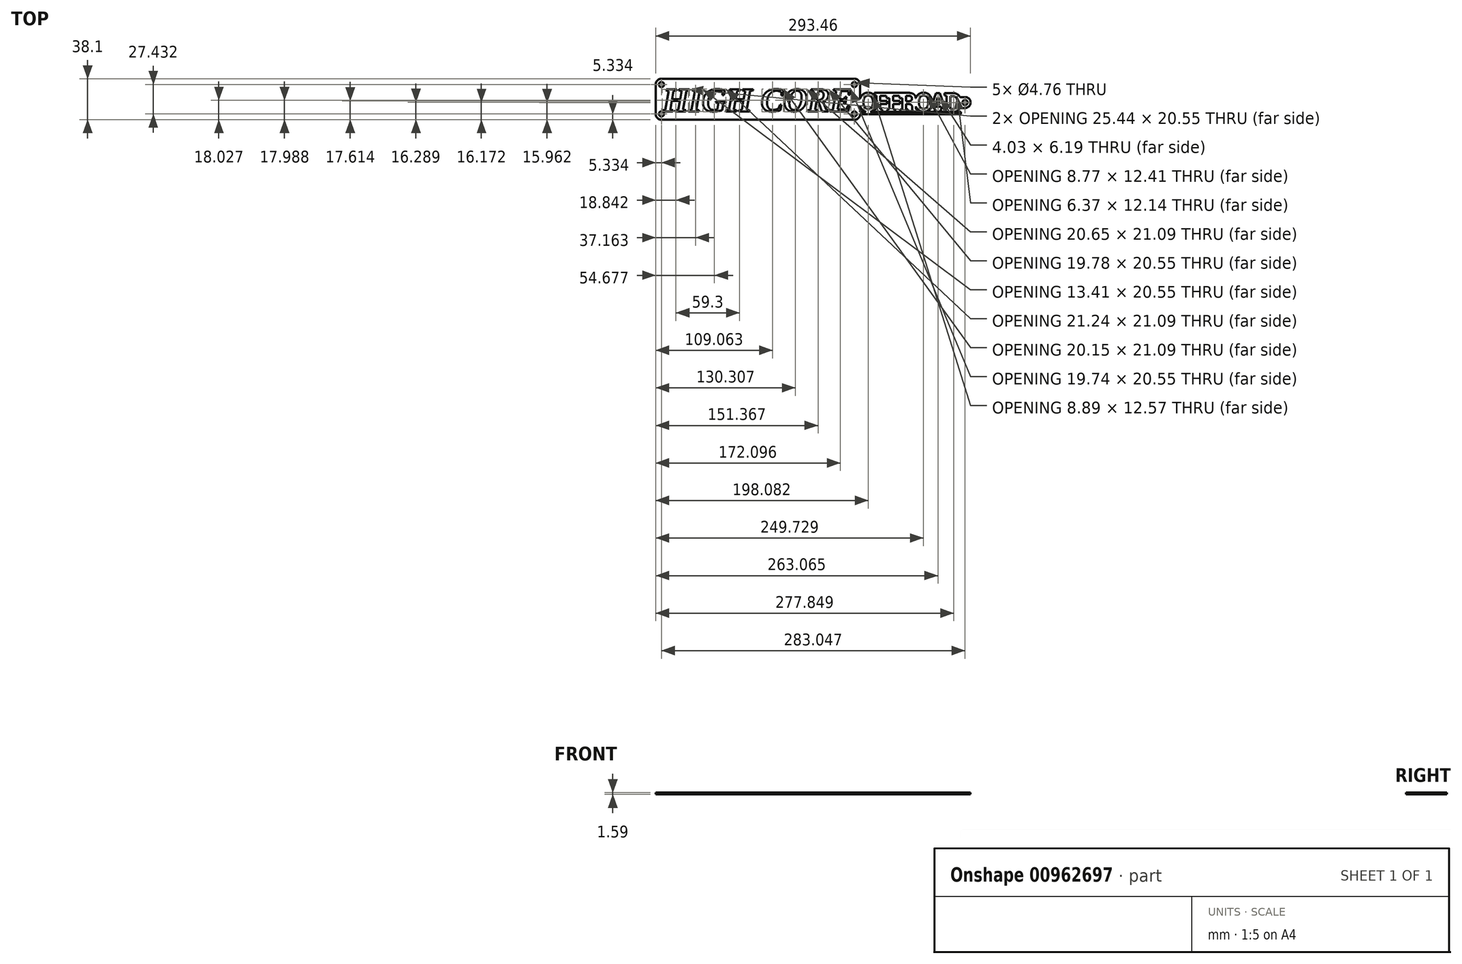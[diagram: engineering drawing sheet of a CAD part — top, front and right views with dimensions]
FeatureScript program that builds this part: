
annotation { "Feature Type Name" : "Feature", "Feature Type Description" : "" }
export const myFeature = defineFeature(function(context is Context, id is Id, definition is map)
    precondition{}
    {
        {
            var Q0;
            Q0=qCreatedBy(makeId("Top.planeOp"),FACE);
            var sketch = newSketch(context, id + "F0", { "sketchPlane" : qUnion([Q0])});
            skLineSegment(sketch, "E0.bottom", {"start": v(95.25, -19.05) * mm, "end": v(-95.25, -19.05) * mm});
            skLineSegment(sketch, "E0.top", {"start": v(95.25, 19.05) * mm, "end": v(-95.25, 19.05) * mm});
            skLineSegment(sketch, "E0.left", {"start": v(95.25, -19.05) * mm, "end": v(95.25, 19.05) * mm});
            skLineSegment(sketch, "E0.right", {"start": v(-95.25, -19.05) * mm, "end": v(-95.25, 19.05) * mm});
            skPoint(sketch, "E0.middle", {"position": v(0, 0) * mm});
            skSolve(sketch);
        }
        {
            var Q0;
            Q0=makeQuery(id+"F0.imprint","IMPRINT",FACE,{"disambiguationData":[TD([[makeQuery(id+"F0.imprint","IMPRINT",EDGE,{"derivedFrom":sQuery(id+"F0.wireOp",EDGE,"E0.bottom")}),-1.0]])]});
            extrude(context, id + "F1", {"entities" : qUnion([Q0]), "depth" : 1.59 * mm, "offsetDistance" : 25.4 * mm});
        }
        {
            var Q0;
            Q0=makeQuery(id+"F1.opExtrude","CAP_FACE",FACE,{"disambiguationData":[OSD([sQuery(id+"F0.wireOp",EDGE,"E0.bottom"),sQuery(id+"F0.wireOp",EDGE,"E0.top"),sQuery(id+"F0.wireOp",EDGE,"E0.left"),sQuery(id+"F0.wireOp",EDGE,"E0.right")])],"isStart":false});
            var sketch = newSketch(context, id + "F2", { "sketchPlane" : qUnion([Q0])});
            skText(sketch, "E1", { "text": "HIGH CORE", "fontName": "Tinos-BoldItalic.ttf"});
            skPoint(sketch, "E2", {"position": v(0, 0) * mm});
            skLineSegment(sketch, "E3", {"start": v(-89.92, 0) * mm, "end": v(0, 0) * mm, "construction": true});
            skLineSegment(sketch, "E4", {"start": v(0, 0) * mm, "end": v(89.92, 0) * mm, "construction": true});
            skLineSegment(sketch, "E5", {"start": v(-95.25, 19.05) * mm, "end": v(-88.39, 12.19) * mm, "construction": true});
            skLineSegment(sketch, "E6", {"start": v(-89.92, 0) * mm, "end": v(-89.92, 13.72) * mm, "construction": true});
            skCircle(sketch, "E7", {"center": v(-89.92, 13.72) * mm, "radius": 2.38 * mm});
            skCircle(sketch, "E8.MirrorC", {"center": v(-89.92, -13.72) * mm, "radius": 2.38 * mm});
            skCircle(sketch, "E9.MirrorC", {"center": v(89.92, 13.72) * mm, "radius": 2.38 * mm});
            skCircle(sketch, "E10.MirrorC", {"center": v(89.92, -13.72) * mm, "radius": 2.38 * mm});
            const initialGuessF2  = {"E1": [-0.0889, -0.0113, 1, 0, 0.0226]};
            skSetInitialGuess(sketch, initialGuessF2);
            skSolve(sketch);
        }
        {
            var Q0;
            Q0=qSketchRegion(id+"F2",true);
            extrude(context, id + "F3", {"entities" : qUnion([Q0]), "operationType" : NewBodyOperationType.REMOVE, "oppositeDirection" : true, "depth" : 25.4 * mm, "offsetDistance" : 25.4 * mm});
        }
        {
            var Q0;
            Q0=makeQuery(id+"F1.opExtrude","SWEPT_EDGE",EDGE,{"disambiguationData":[OSD([sQuery(id+"F0.wireOp",EDGE,"E0.top"),sQuery(id+"F0.wireOp",EDGE,"E0.right")])]});
            var Q1;
            Q1=makeQuery(id+"F1.opExtrude","SWEPT_EDGE",EDGE,{"disambiguationData":[OSD([sQuery(id+"F0.wireOp",EDGE,"E0.bottom"),sQuery(id+"F0.wireOp",EDGE,"E0.right")])]});
            var Q2;
            Q2=makeQuery(id+"F1.opExtrude","SWEPT_EDGE",EDGE,{"disambiguationData":[OSD([sQuery(id+"F0.wireOp",EDGE,"E0.top"),sQuery(id+"F0.wireOp",EDGE,"E0.left")])]});
            var Q3;
            Q3=makeQuery(id+"F1.opExtrude","SWEPT_EDGE",EDGE,{"disambiguationData":[OSD([sQuery(id+"F0.wireOp",EDGE,"E0.bottom"),sQuery(id+"F0.wireOp",EDGE,"E0.left")])]});
            fillet(context, id + "F4", {"entities" : qUnion([Q0, Q1, Q2, Q3]), "radius" : 5.08 * mm, "tangentPropagation" : true, "allowEdgeOverflow" : false});
        }
        {
            var Q0;
            Q0=makeQuery(id+"F1.opExtrude","CAP_FACE",FACE,{"disambiguationData":[OSD([sQuery(id+"F0.wireOp",EDGE,"E0.bottom"),sQuery(id+"F0.wireOp",EDGE,"E0.top"),sQuery(id+"F0.wireOp",EDGE,"E0.left"),sQuery(id+"F0.wireOp",EDGE,"E0.right")])],"isStart":false});
            var sketch = newSketch(context, id + "F5", { "sketchPlane" : qUnion([Q0])});
            skPoint(sketch, "E11", {"position": v(93.37, -3.45) * mm});
            skText(sketch, "E12", { "text": "O", "fontName": "RobotoSlab-Bold.ttf"});
            skText(sketch, "E13", { "text": "F", "fontName": "RobotoSlab-Bold.ttf"});
            skText(sketch, "E14", { "text": "F", "fontName": "RobotoSlab-Bold.ttf"});
            skText(sketch, "E15", { "text": "R", "fontName": "RobotoSlab-Bold.ttf"});
            skText(sketch, "E16", { "text": "O", "fontName": "RobotoSlab-Bold.ttf"});
            skText(sketch, "E17", { "text": "A", "fontName": "RobotoSlab-Bold.ttf"});
            skText(sketch, "E18", { "text": "D", "fontName": "RobotoSlab-Bold.ttf"});
            skLineSegment(sketch, "E19", {"start": v(87.12, -11.65) * mm, "end": v(189.23, -11.65) * mm});
            skLineSegment(sketch, "E20.0", {"start": v(95.25, -13.97) * mm, "end": v(95.25, 13.97) * mm});
            skLineSegment(sketch, "E21", {"start": v(95.25, -13.97) * mm, "end": v(189.23, -13.97) * mm});
            skLineSegment(sketch, "E22", {"start": v(189.23, -11.65) * mm, "end": v(189.23, -13.97) * mm});
            skLineSegment(sketch, "E23", {"start": v(95.25, -13.97) * mm, "end": v(95.25, -11.65) * mm});
            skLineSegment(sketch, "E24", {"start": v(95.25, -11.65) * mm, "end": v(189.23, -11.65) * mm});
            const initialGuessF5  = {"E12": [0.09406, -0.01165, 1, 0, 0.01778], "E13": [0.10804, -0.01165, 1, 0, 0.01778], "E14": [0.12013, -0.01165, 1, 0, 0.01778], "E15": [0.1322, -0.01165, 1, 0, 0.01778], "E16": [0.14582, -0.01142, 1, 0, 0.01755], "E17": [0.15894, -0.01186, 1, 0, 0.01778], "E18": [0.17335, -0.01186, 1, 0, 0.01778]};
            skSetInitialGuess(sketch, initialGuessF5);
            skSolve(sketch);
        }
        {
            var Q0;
            {var subQ2=sQuery(id+"F5.wireOp",EDGE,"E17.sketch_text.stroke-5");Q0=makeQuery(id+"F5.imprint","IMPRINT",FACE,{"disambiguationData":[TD([[makeQuery(id+"F5.imprint","IMPRINT",EDGE,{"derivedFrom":subQ2}),-1.0]])]});}
            var Q1;
            {var subQ6=sQuery(id+"F5.wireOp",EDGE,"E17.sketch_text.stroke-5");Q1=makeQuery(id+"F5.imprint","IMPRINT",FACE,{"disambiguationData":[TD([[makeQuery(id+"F5.imprint","IMPRINT",EDGE,{"derivedFrom":subQ6}),1.0]])]});}
            var Q2;
            {var subQ15=sQuery(id+"F5.wireOp",EDGE,"E17.sketch_text.stroke-2");Q2=makeQuery(id+"F5.imprint","IMPRINT",FACE,{"disambiguationData":[TD([[makeQuery(id+"F5.imprint","IMPRINT",EDGE,{"derivedFrom":subQ15}),-1.0]])]});}
            var Q3;
            {var subQ0=sQuery(id+"F5.wireOp",EDGE,"E16.sketch_text.stroke-1");var subQ1=sQuery(id+"F5.wireOp",EDGE,"E16.sketch_text.stroke-0");var subQ2=makeQuery(id+"F5.imprint","INTERSECT",VERTEX,{"derivedFrom":[subQ1,subQ0]});Q3=makeQuery(id+"F5.imprint","IMPRINT",FACE,{"disambiguationData":[TD([[makeQuery(id+"F5.imprint","IMPRINT",EDGE,{"disambiguationData":[TD([[subQ2,1.0]])],"derivedFrom":subQ1}),1.0]])]});}
            var Q4;
            {var subQ0=sQuery(id+"F5.wireOp",EDGE,"E17.sketch_text.stroke-15");var subQ1=sQuery(id+"F5.wireOp",EDGE,"E16.sketch_text.stroke-1");var subQ2=makeQuery(id+"F5.imprint","INTERSECT",VERTEX,{"derivedFrom":[subQ1,subQ0]});Q4=makeQuery(id+"F5.imprint","IMPRINT",FACE,{"disambiguationData":[TD([[makeQuery(id+"F5.imprint","IMPRINT",EDGE,{"disambiguationData":[TD([[subQ2,1.0]])],"derivedFrom":subQ1}),-1.0]])]});}
            var Q5;
            {var subQ9=sQuery(id+"F5.wireOp",EDGE,"E16.sketch_text.stroke-4");Q5=makeQuery(id+"F5.imprint","IMPRINT",FACE,{"disambiguationData":[TD([[makeQuery(id+"F5.imprint","IMPRINT",EDGE,{"derivedFrom":subQ9}),-1.0]])]});}
            var Q6;
            {var subQ0=sQuery(id+"F5.wireOp",EDGE,"E17.sketch_text.stroke-1");var subQ1=sQuery(id+"F5.wireOp",EDGE,"E16.sketch_text.stroke-0");var subQ2=makeQuery(id+"F5.imprint","INTERSECT",VERTEX,{"disambiguationData":[OD(0.0)],"derivedFrom":[subQ1,subQ0]});Q6=makeQuery(id+"F5.imprint","IMPRINT",FACE,{"disambiguationData":[TD([[makeQuery(id+"F5.imprint","IMPRINT",EDGE,{"disambiguationData":[TD([[subQ2,-1.0]])],"derivedFrom":subQ1}),-1.0]])]});}
            var Q7;
            {var subQ7=sQuery(id+"F5.wireOp",EDGE,"E14.sketch_text.stroke-5");Q7=makeQuery(id+"F5.imprint","IMPRINT",FACE,{"disambiguationData":[TD([[makeQuery(id+"F5.imprint","IMPRINT",EDGE,{"derivedFrom":subQ7}),1.0]])]});}
            var Q8;
            {var subQ0=sQuery(id+"F5.wireOp",EDGE,"E15.sketch_text.stroke-2");var subQ1=sQuery(id+"F5.wireOp",EDGE,"E15.sketch_text.stroke-1");var subQ2=makeQuery(id+"F5.imprint","INTERSECT",VERTEX,{"derivedFrom":[subQ1,subQ0]});Q8=makeQuery(id+"F5.imprint","IMPRINT",FACE,{"disambiguationData":[TD([[makeQuery(id+"F5.imprint","IMPRINT",EDGE,{"disambiguationData":[TD([[subQ2,1.0]])],"derivedFrom":subQ1}),-1.0]])]});}
            var Q9;
            {var subQ0=sQuery(id+"F5.wireOp",EDGE,"E16.sketch_text.stroke-3");var subQ1=sQuery(id+"F5.wireOp",EDGE,"E15.sketch_text.stroke-5");var subQ2=makeQuery(id+"F5.imprint","INTERSECT",VERTEX,{"disambiguationData":[OD(0.0)],"derivedFrom":[subQ1,subQ0]});Q9=makeQuery(id+"F5.imprint","IMPRINT",FACE,{"disambiguationData":[TD([[makeQuery(id+"F5.imprint","IMPRINT",EDGE,{"disambiguationData":[TD([[subQ2,-1.0]])],"derivedFrom":subQ1}),-1.0]])]});}
            var Q10;
            {var subQ2=sQuery(id+"F5.wireOp",EDGE,"E14.sketch_text.stroke-5");Q10=makeQuery(id+"F5.imprint","IMPRINT",FACE,{"disambiguationData":[TD([[makeQuery(id+"F5.imprint","IMPRINT",EDGE,{"derivedFrom":subQ2}),-1.0]])]});}
            var Q11;
            {var subQ1=sQuery(id+"F5.wireOp",EDGE,"E13.sketch_text.stroke-5");Q11=makeQuery(id+"F5.imprint","IMPRINT",FACE,{"disambiguationData":[TD([[makeQuery(id+"F5.imprint","IMPRINT",EDGE,{"derivedFrom":subQ1}),1.0]])]});}
            var Q12;
            {var subQ2=sQuery(id+"F5.wireOp",EDGE,"E13.sketch_text.stroke-5");Q12=makeQuery(id+"F5.imprint","IMPRINT",FACE,{"disambiguationData":[TD([[makeQuery(id+"F5.imprint","IMPRINT",EDGE,{"derivedFrom":subQ2}),-1.0]])]});}
            var Q13;
            {var subQ8=sQuery(id+"F5.wireOp",EDGE,"E12.sketch_text.stroke-9");Q13=makeQuery(id+"F5.imprint","IMPRINT",FACE,{"disambiguationData":[TD([[makeQuery(id+"F5.imprint","IMPRINT",EDGE,{"derivedFrom":subQ8}),1.0]])]});}
            var Q14;
            {var subQ0=sQuery(id+"F5.wireOp",EDGE,"E12.sketch_text.stroke-6");Q14=makeQuery(id+"F5.imprint","IMPRINT",FACE,{"disambiguationData":[TD([[makeQuery(id+"F5.imprint","IMPRINT",EDGE,{"derivedFrom":subQ0}),-1.0]])]});}
            var Q15;
            {var subQ5=sQuery(id+"F5.wireOp",EDGE,"E15.sketch_text.stroke-3");Q15=makeQuery(id+"F5.imprint","IMPRINT",FACE,{"disambiguationData":[TD([[makeQuery(id+"F5.imprint","IMPRINT",EDGE,{"derivedFrom":subQ5}),1.0]])]});}
            var Q16;
            Q16=makeQuery(id+"F5.imprint","IMPRINT",FACE,{"disambiguationData":[TD([[makeQuery(id+"F5.imprint","IMPRINT",EDGE,{"derivedFrom":sQuery(id+"F5.wireOp",EDGE,"E18.sketch_text.stroke-0")}),-1.0]])]});
            var Q17;
            {var subQ3=sQuery(id+"F5.wireOp",EDGE,"E17.sketch_text.stroke-4");var subQ5=sQuery(id+"F5.wireOp",EDGE,"E17.sketch_text.stroke-5");var subQ6=makeQuery(id+"F5.imprint","INTERSECT",VERTEX,{"derivedFrom":[subQ3,subQ5]});Q17=makeQuery(id+"F5.imprint","IMPRINT",FACE,{"disambiguationData":[TD([[makeQuery(id+"F5.imprint","IMPRINT",EDGE,{"disambiguationData":[TD([[subQ6,1.0]])],"derivedFrom":subQ3}),-1.0]])]});}
            extrude(context, id + "F6", {"entities" : qUnion([Q0, Q1, Q2, Q3, Q4, Q5, Q6, Q7, Q8, Q9, Q10, Q11, Q12, Q13, Q14, Q15, Q16, Q17]), "operationType" : NewBodyOperationType.ADD, "oppositeDirection" : true, "depth" : 1.59 * mm, "offsetDistance" : 25.4 * mm});
        }
        {
            var Q0;
            Q0=makeQuery(id+"F6.opExtrude","CAP_FACE",FACE,{"disambiguationData":[OSD([sQuery(id+"F5.wireOp",EDGE,"E12.sketch_text.stroke-0"),sQuery(id+"F5.wireOp",EDGE,"E12.sketch_text.stroke-8"),sQuery(id+"F5.wireOp",EDGE,"E12.sketch_text.stroke-9"),sQuery(id+"F5.wireOp",EDGE,"E13.sketch_text.stroke-0"),sQuery(id+"F5.wireOp",EDGE,"E13.sketch_text.stroke-1"),sQuery(id+"F5.wireOp",EDGE,"E13.sketch_text.stroke-2"),sQuery(id+"F5.wireOp",EDGE,"E13.sketch_text.stroke-3"),sQuery(id+"F5.wireOp",EDGE,"E13.sketch_text.stroke-4"),sQuery(id+"F5.wireOp",EDGE,"E13.sketch_text.stroke-6"),sQuery(id+"F5.wireOp",EDGE,"E13.sketch_text.stroke-7"),sQuery(id+"F5.wireOp",EDGE,"E13.sketch_text.stroke-8"),sQuery(id+"F5.wireOp",EDGE,"E13.sketch_text.stroke-9"),sQuery(id+"F5.wireOp",EDGE,"E13.sketch_text.stroke-10"),sQuery(id+"F5.wireOp",EDGE,"E13.sketch_text.stroke-11"),sQuery(id+"F5.wireOp",EDGE,"E13.sketch_text.stroke-12"),sQuery(id+"F5.wireOp",EDGE,"E13.sketch_text.stroke-13"),sQuery(id+"F5.wireOp",EDGE,"E13.sketch_text.stroke-14"),sQuery(id+"F5.wireOp",EDGE,"E13.sketch_text.stroke-15"),sQuery(id+"F5.wireOp",EDGE,"E13.sketch_text.stroke-17"),sQuery(id+"F5.wireOp",EDGE,"E14.sketch_text.stroke-0"),sQuery(id+"F5.wireOp",EDGE,"E14.sketch_text.stroke-1"),sQuery(id+"F5.wireOp",EDGE,"E14.sketch_text.stroke-4"),sQuery(id+"F5.wireOp",EDGE,"E14.sketch_text.stroke-6"),sQuery(id+"F5.wireOp",EDGE,"E14.sketch_text.stroke-7"),sQuery(id+"F5.wireOp",EDGE,"E14.sketch_text.stroke-8"),sQuery(id+"F5.wireOp",EDGE,"E14.sketch_text.stroke-9"),sQuery(id+"F5.wireOp",EDGE,"E14.sketch_text.stroke-10"),sQuery(id+"F5.wireOp",EDGE,"E14.sketch_text.stroke-11"),sQuery(id+"F5.wireOp",EDGE,"E14.sketch_text.stroke-12"),sQuery(id+"F5.wireOp",EDGE,"E14.sketch_text.stroke-13"),sQuery(id+"F5.wireOp",EDGE,"E14.sketch_text.stroke-14"),sQuery(id+"F5.wireOp",EDGE,"E14.sketch_text.stroke-15"),sQuery(id+"F5.wireOp",EDGE,"E14.sketch_text.stroke-17"),sQuery(id+"F5.wireOp",EDGE,"E15.sketch_text.stroke-0"),sQuery(id+"F5.wireOp",EDGE,"E15.sketch_text.stroke-1"),sQuery(id+"F5.wireOp",EDGE,"E15.sketch_text.stroke-5"),sQuery(id+"F5.wireOp",EDGE,"E15.sketch_text.stroke-6"),sQuery(id+"F5.wireOp",EDGE,"E15.sketch_text.stroke-7"),sQuery(id+"F5.wireOp",EDGE,"E15.sketch_text.stroke-8"),sQuery(id+"F5.wireOp",EDGE,"E15.sketch_text.stroke-9"),sQuery(id+"F5.wireOp",EDGE,"E15.sketch_text.stroke-10"),sQuery(id+"F5.wireOp",EDGE,"E15.sketch_text.stroke-12"),sQuery(id+"F5.wireOp",EDGE,"E15.sketch_text.stroke-13"),sQuery(id+"F5.wireOp",EDGE,"E15.sketch_text.stroke-14"),sQuery(id+"F5.wireOp",EDGE,"E15.sketch_text.stroke-15"),sQuery(id+"F5.wireOp",EDGE,"E15.sketch_text.stroke-16"),sQuery(id+"F5.wireOp",EDGE,"E15.sketch_text.stroke-17"),sQuery(id+"F5.wireOp",EDGE,"E15.sketch_text.stroke-18"),sQuery(id+"F5.wireOp",EDGE,"E15.sketch_text.stroke-19"),sQuery(id+"F5.wireOp",EDGE,"E15.sketch_text.stroke-20"),sQuery(id+"F5.wireOp",EDGE,"E15.sketch_text.stroke-22"),sQuery(id+"F5.wireOp",EDGE,"E15.sketch_text.stroke-23"),sQuery(id+"F5.wireOp",EDGE,"E15.sketch_text.stroke-24"),sQuery(id+"F5.wireOp",EDGE,"E15.sketch_text.stroke-27"),sQuery(id+"F5.wireOp",EDGE,"E15.sketch_text.stroke-28"),sQuery(id+"F5.wireOp",EDGE,"E15.sketch_text.stroke-29"),sQuery(id+"F5.wireOp",EDGE,"E15.sketch_text.stroke-30"),sQuery(id+"F5.wireOp",EDGE,"E15.sketch_text.stroke-31"),sQuery(id+"F5.wireOp",EDGE,"E15.sketch_text.stroke-32"),sQuery(id+"F5.wireOp",EDGE,"E15.sketch_text.stroke-33"),sQuery(id+"F5.wireOp",EDGE,"E15.sketch_text.stroke-34"),sQuery(id+"F5.wireOp",EDGE,"E15.sketch_text.stroke-35"),sQuery(id+"F5.wireOp",EDGE,"E16.sketch_text.stroke-0"),sQuery(id+"F5.wireOp",EDGE,"E16.sketch_text.stroke-1"),sQuery(id+"F5.wireOp",EDGE,"E16.sketch_text.stroke-2"),sQuery(id+"F5.wireOp",EDGE,"E16.sketch_text.stroke-3"),sQuery(id+"F5.wireOp",EDGE,"E16.sketch_text.stroke-5"),sQuery(id+"F5.wireOp",EDGE,"E16.sketch_text.stroke-6"),sQuery(id+"F5.wireOp",EDGE,"E16.sketch_text.stroke-7"),sQuery(id+"F5.wireOp",EDGE,"E16.sketch_text.stroke-8"),sQuery(id+"F5.wireOp",EDGE,"E16.sketch_text.stroke-9"),sQuery(id+"F5.wireOp",EDGE,"E16.sketch_text.stroke-10"),sQuery(id+"F5.wireOp",EDGE,"E16.sketch_text.stroke-11"),sQuery(id+"F5.wireOp",EDGE,"E16.sketch_text.stroke-12"),sQuery(id+"F5.wireOp",EDGE,"E16.sketch_text.stroke-13"),sQuery(id+"F5.wireOp",EDGE,"E16.sketch_text.stroke-14"),sQuery(id+"F5.wireOp",EDGE,"E16.sketch_text.stroke-15"),sQuery(id+"F5.wireOp",EDGE,"E16.sketch_text.stroke-16"),sQuery(id+"F5.wireOp",EDGE,"E16.sketch_text.stroke-17"),sQuery(id+"F5.wireOp",EDGE,"E16.sketch_text.stroke-18"),sQuery(id+"F5.wireOp",EDGE,"E16.sketch_text.stroke-19"),sQuery(id+"F5.wireOp",EDGE,"E17.sketch_text.stroke-1"),sQuery(id+"F5.wireOp",EDGE,"E17.sketch_text.stroke-2"),sQuery(id+"F5.wireOp",EDGE,"E17.sketch_text.stroke-3"),sQuery(id+"F5.wireOp",EDGE,"E17.sketch_text.stroke-4"),sQuery(id+"F5.wireOp",EDGE,"E17.sketch_text.stroke-6"),sQuery(id+"F5.wireOp",EDGE,"E17.sketch_text.stroke-7"),sQuery(id+"F5.wireOp",EDGE,"E17.sketch_text.stroke-8"),sQuery(id+"F5.wireOp",EDGE,"E17.sketch_text.stroke-9"),sQuery(id+"F5.wireOp",EDGE,"E17.sketch_text.stroke-10"),sQuery(id+"F5.wireOp",EDGE,"E17.sketch_text.stroke-11"),sQuery(id+"F5.wireOp",EDGE,"E17.sketch_text.stroke-12"),sQuery(id+"F5.wireOp",EDGE,"E17.sketch_text.stroke-13"),sQuery(id+"F5.wireOp",EDGE,"E17.sketch_text.stroke-14"),sQuery(id+"F5.wireOp",EDGE,"E17.sketch_text.stroke-15"),sQuery(id+"F5.wireOp",EDGE,"E17.sketch_text.stroke-16"),sQuery(id+"F5.wireOp",EDGE,"E17.sketch_text.stroke-17"),sQuery(id+"F5.wireOp",EDGE,"E17.sketch_text.stroke-18"),sQuery(id+"F5.wireOp",EDGE,"E17.sketch_text.stroke-19"),sQuery(id+"F5.wireOp",EDGE,"E18.sketch_text.stroke-0"),sQuery(id+"F5.wireOp",EDGE,"E18.sketch_text.stroke-1"),sQuery(id+"F5.wireOp",EDGE,"E18.sketch_text.stroke-2"),sQuery(id+"F5.wireOp",EDGE,"E18.sketch_text.stroke-3"),sQuery(id+"F5.wireOp",EDGE,"E18.sketch_text.stroke-4"),sQuery(id+"F5.wireOp",EDGE,"E18.sketch_text.stroke-5"),sQuery(id+"F5.wireOp",EDGE,"E18.sketch_text.stroke-7"),sQuery(id+"F5.wireOp",EDGE,"E18.sketch_text.stroke-8"),sQuery(id+"F5.wireOp",EDGE,"E18.sketch_text.stroke-9"),sQuery(id+"F5.wireOp",EDGE,"E18.sketch_text.stroke-10"),sQuery(id+"F5.wireOp",EDGE,"E18.sketch_text.stroke-11"),sQuery(id+"F5.wireOp",EDGE,"E18.sketch_text.stroke-12"),sQuery(id+"F5.wireOp",EDGE,"E18.sketch_text.stroke-13"),sQuery(id+"F5.wireOp",EDGE,"E18.sketch_text.stroke-14"),sQuery(id+"F5.wireOp",EDGE,"E18.sketch_text.stroke-15"),sQuery(id+"F5.wireOp",EDGE,"E18.sketch_text.stroke-16"),sQuery(id+"F5.wireOp",EDGE,"E18.sketch_text.stroke-17"),sQuery(id+"F5.wireOp",EDGE,"E18.sketch_text.stroke-18"),sQuery(id+"F5.wireOp",EDGE,"E18.sketch_text.stroke-19"),sQuery(id+"F5.wireOp",EDGE,"E18.sketch_text.stroke-20"),sQuery(id+"F5.wireOp",EDGE,"E24")])],"isStart":true});
            var sketch = newSketch(context, id + "F7", { "sketchPlane" : qUnion([Q0])});
            skLineSegment(sketch, "E25", {"start": v(189.32, -3.09) * mm, "end": v(193.13, -3.09) * mm, "construction": true});
            skCircle(sketch, "E26", {"center": v(193.13, -3.09) * mm, "radius": 2.38 * mm});
            skCircle(sketch, "E27", {"center": v(193.13, -3.09) * mm, "radius": 5.08 * mm});
            skLineSegment(sketch, "E28", {"start": v(193.13, 2) * mm, "end": v(187.45, 2) * mm});
            skLineSegment(sketch, "E29", {"start": v(193.13, -8.17) * mm, "end": v(187.5, -8.17) * mm});
            skLineSegment(sketch, "E30", {"start": v(187.5, -8.17) * mm, "end": v(187.45, 2) * mm});
            skSolve(sketch);
        }
        {
            var Q0;
            Q0=makeQuery(id+"F5.imprint","IMPRINT",FACE,{"disambiguationData":[TD([[makeQuery(id+"F5.imprint","IMPRINT",EDGE,{"derivedFrom":sQuery(id+"F5.wireOp",EDGE,"E21")}),1.0]])]});
            var Q1;
            {var subQ0=sQuery(id+"F5.wireOp",EDGE,"E12.sketch_text.stroke-2");var subQ1=sQuery(id+"F5.wireOp",EDGE,"E12.sketch_text.stroke-1");var subQ2=makeQuery(id+"F5.imprint","INTERSECT",VERTEX,{"derivedFrom":[subQ1,subQ0]});Q1=makeQuery(id+"F5.imprint","IMPRINT",FACE,{"disambiguationData":[TD([[makeQuery(id+"F5.imprint","IMPRINT",EDGE,{"disambiguationData":[TD([[subQ2,1.0]])],"derivedFrom":subQ1}),-1.0]])]});}
            var Q2;
            {var subQ0=sQuery(id+"F7.wireOp",EDGE,"E28");var subQ1=sQuery(id+"F7.wireOp",EDGE,"E27");var subQ2=makeQuery(id+"F7.imprint","INTERSECT",VERTEX,{"derivedFrom":[subQ1,subQ0]});Q2=makeQuery(id+"F7.imprint","IMPRINT",FACE,{"disambiguationData":[TD([[makeQuery(id+"F7.imprint","IMPRINT",EDGE,{"disambiguationData":[TD([[subQ2,-1.0]])],"derivedFrom":subQ1}),-1.0]])]});}
            var Q3;
            Q3=makeQuery(id+"F7.imprint","IMPRINT",FACE,{"disambiguationData":[TD([[makeQuery(id+"F7.imprint","IMPRINT",EDGE,{"derivedFrom":sQuery(id+"F7.wireOp",EDGE,"E26")}),-1.0]])]});
            var Q4;
            {var subQ0=sQuery(id+"F7.wireOp",EDGE,"E29");var subQ1=sQuery(id+"F7.wireOp",EDGE,"E27");var subQ2=makeQuery(id+"F7.imprint","INTERSECT",VERTEX,{"derivedFrom":[subQ1,subQ0]});Q4=makeQuery(id+"F7.imprint","IMPRINT",FACE,{"disambiguationData":[TD([[makeQuery(id+"F7.imprint","IMPRINT",EDGE,{"disambiguationData":[TD([[subQ2,1.0]])],"derivedFrom":subQ1}),-1.0]])]});}
            extrude(context, id + "F8", {"entities" : qUnion([Q0, Q1, Q2, Q3, Q4]), "operationType" : NewBodyOperationType.ADD, "oppositeDirection" : true, "depth" : 1.59 * mm, "offsetDistance" : 25.4 * mm});
        }
    });
